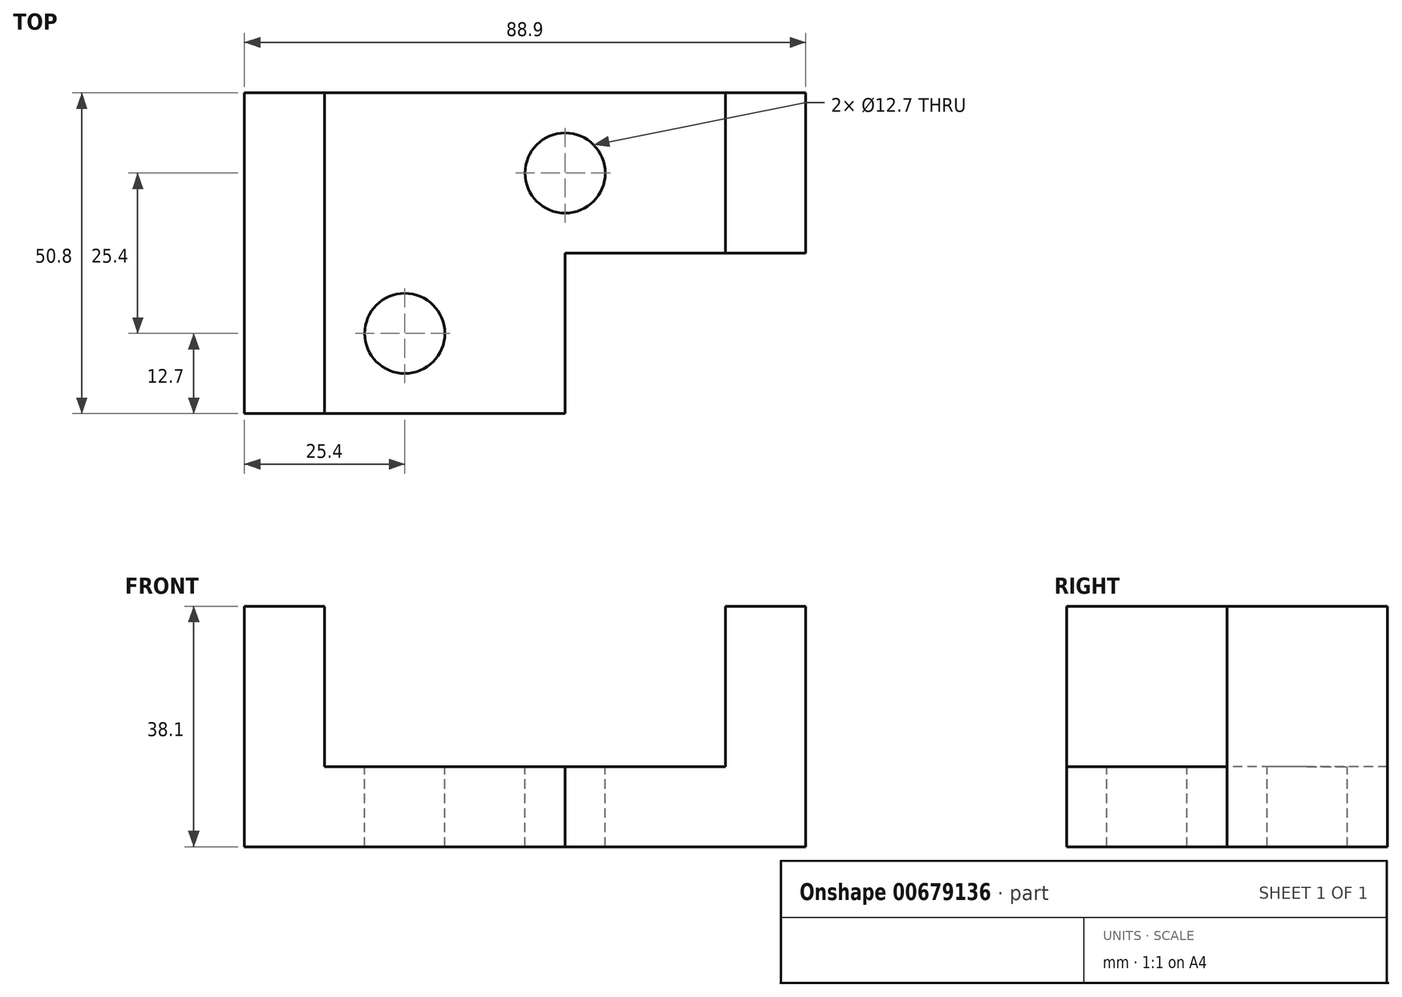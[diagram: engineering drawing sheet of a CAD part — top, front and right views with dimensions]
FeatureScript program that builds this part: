
annotation { "Feature Type Name" : "Feature", "Feature Type Description" : "" }
export const myFeature = defineFeature(function(context is Context, id is Id, definition is map)
    precondition{}
    {
        {
            var Q0;
            Q0=qCreatedBy(makeId("Front.planeOp"),FACE);
            var sketch = newSketch(context, id + "F0", { "sketchPlane" : qUnion([Q0])});
            skLineSegment(sketch, "E0.bottom", {"start": v(-44.45, 19.05) * mm, "end": v(44.45, 19.05) * mm});
            skLineSegment(sketch, "E0.top", {"start": v(-44.45, -19.05) * mm, "end": v(44.45, -19.05) * mm});
            skLineSegment(sketch, "E0.left", {"start": v(-44.45, 19.05) * mm, "end": v(-44.45, -19.05) * mm});
            skLineSegment(sketch, "E0.right", {"start": v(44.45, 19.05) * mm, "end": v(44.45, -19.05) * mm});
            skPoint(sketch, "E0.middle", {"position": v(0, 0) * mm});
            skSolve(sketch);
        }
        {
            var Q0;
            Q0=makeQuery(id+"F0.imprint","IMPRINT",FACE,{"disambiguationData":[TD([[makeQuery(id+"F0.imprint","IMPRINT",EDGE,{"derivedFrom":sQuery(id+"F0.wireOp",EDGE,"E0.bottom")}),-1.0]])]});
            extrude(context, id + "F1", {"entities" : qUnion([Q0]), "depth" : 50.8 * mm, "offsetDistance" : 25.4 * mm});
        }
        {
            var Q0;
            Q0=makeQuery(id+"F1.opExtrude","CAP_FACE",FACE,{"disambiguationData":[OSD([sQuery(id+"F0.wireOp",EDGE,"E0.bottom"),sQuery(id+"F0.wireOp",EDGE,"E0.top"),sQuery(id+"F0.wireOp",EDGE,"E0.left"),sQuery(id+"F0.wireOp",EDGE,"E0.right")])],"isStart":false});
            var sketch = newSketch(context, id + "F2", { "sketchPlane" : qUnion([Q0])});
            skLineSegment(sketch, "E1.bottom", {"start": v(-31.75, 19.05) * mm, "end": v(31.75, 19.05) * mm});
            skLineSegment(sketch, "E1.top", {"start": v(-31.75, 0) * mm, "end": v(31.75, 0) * mm});
            skLineSegment(sketch, "E1.left", {"start": v(-31.75, 19.05) * mm, "end": v(-31.75, 0) * mm});
            skLineSegment(sketch, "E1.right", {"start": v(31.75, 19.05) * mm, "end": v(31.75, 0) * mm});
            skSolve(sketch);
        }
        {
            var Q0;
            Q0=makeQuery(id+"F2.imprint","IMPRINT",FACE,{"disambiguationData":[TD([[makeQuery(id+"F2.imprint","IMPRINT",EDGE,{"derivedFrom":sQuery(id+"F2.wireOp",EDGE,"E1.bottom")}),-1.0]])]});
            extrude(context, id + "F3", {"entities" : qUnion([Q0]), "operationType" : NewBodyOperationType.REMOVE, "endBound" : BoundingType.THROUGH_ALL, "oppositeDirection" : true, "depth" : 25.4 * mm, "offsetDistance" : 25.4 * mm});
        }
        {
            var Q0;
            {var subQ0=sQuery(id+"F0.wireOp",EDGE,"E0.right");var subQ3=sQuery(id+"F0.wireOp",EDGE,"E0.bottom");Q0=makeQuery(id+"F3.boolean.opBoolean","SPLIT",FACE,{"disambiguationData":[TD([makeQuery(id+"F1.opExtrude","SWEPT_FACE",FACE,{"disambiguationData":[OSD([subQ0])]})])],"derivedFrom":makeQuery(id+"F1.opExtrude","SWEPT_FACE",FACE,{"disambiguationData":[OSD([subQ3])]})});}
            var sketch = newSketch(context, id + "F4", { "sketchPlane" : qUnion([Q0])});
            skLineSegment(sketch, "E2.bottom", {"start": v(44.45, -50.8) * mm, "end": v(6.35, -50.8) * mm});
            skLineSegment(sketch, "E2.top", {"start": v(44.45, -25.4) * mm, "end": v(6.35, -25.4) * mm});
            skLineSegment(sketch, "E2.left", {"start": v(44.45, -50.8) * mm, "end": v(44.45, -25.4) * mm});
            skLineSegment(sketch, "E2.right", {"start": v(6.35, -50.8) * mm, "end": v(6.35, -25.4) * mm});
            skSolve(sketch);
        }
        {
            var Q0;
            {var subQ0=sQuery(id+"F4.wireOp",EDGE,"E2.left");Q0=makeQuery(id+"F4.imprint","IMPRINT",FACE,{"disambiguationData":[TD([[makeQuery(id+"F4.imprint","IMPRINT",EDGE,{"derivedFrom":subQ0}),1.0]])]});}
            extrude(context, id + "F5", {"entities" : qUnion([Q0]), "operationType" : NewBodyOperationType.REMOVE, "endBound" : BoundingType.THROUGH_ALL, "oppositeDirection" : true, "depth" : 25.4 * mm, "offsetDistance" : 25.4 * mm});
        }
        {
            var Q0;
            Q0=makeQuery(id+"F3.boolean.opBoolean","COPY",FACE,{"derivedFrom":makeQuery(id+"F3.opExtrude","SWEPT_FACE",FACE,{"disambiguationData":[OSD([sQuery(id+"F2.wireOp",EDGE,"E1.top")])]})});
            var sketch = newSketch(context, id + "F6", { "sketchPlane" : qUnion([Q0])});
            skLineSegment(sketch, "E3.bottom", {"start": v(31.75, -50.8) * mm, "end": v(6.35, -50.8) * mm});
            skLineSegment(sketch, "E3.top", {"start": v(31.75, -25.4) * mm, "end": v(6.35, -25.4) * mm});
            skLineSegment(sketch, "E3.left", {"start": v(31.75, -50.8) * mm, "end": v(31.75, -25.4) * mm});
            skLineSegment(sketch, "E3.right", {"start": v(6.35, -50.8) * mm, "end": v(6.35, -25.4) * mm});
            skSolve(sketch);
        }
        {
            var Q0;
            Q0=makeQuery(id+"F6.imprint","IMPRINT",FACE,{"disambiguationData":[TD([[makeQuery(id+"F6.imprint","IMPRINT",EDGE,{"derivedFrom":sQuery(id+"F6.wireOp",EDGE,"E3.bottom")}),1.0]])]});
            extrude(context, id + "F7", {"entities" : qUnion([Q0]), "operationType" : NewBodyOperationType.REMOVE, "endBound" : BoundingType.THROUGH_ALL, "oppositeDirection" : true, "depth" : 25.4 * mm, "offsetDistance" : 25.4 * mm});
        }
        {
            var Q0;
            Q0=makeQuery(id+"F3.boolean.opBoolean","COPY",FACE,{"derivedFrom":makeQuery(id+"F3.opExtrude","SWEPT_FACE",FACE,{"disambiguationData":[OSD([sQuery(id+"F2.wireOp",EDGE,"E1.top")])]})});
            var sketch = newSketch(context, id + "F8", { "sketchPlane" : qUnion([Q0])});
            skCircle(sketch, "E4", {"center": v(-19.05, -38.1) * mm, "radius": 6.35 * mm});
            skSolve(sketch);
        }
        {
            var Q0;
            Q0=makeQuery(id+"F8.imprint","IMPRINT",FACE,{"disambiguationData":[TD([[makeQuery(id+"F8.imprint","IMPRINT",EDGE,{"derivedFrom":sQuery(id+"F8.wireOp",EDGE,"E4")}),1.0]])]});
            extrude(context, id + "F9", {"entities" : qUnion([Q0]), "operationType" : NewBodyOperationType.REMOVE, "endBound" : BoundingType.THROUGH_ALL, "oppositeDirection" : true, "depth" : 25.4 * mm, "offsetDistance" : 25.4 * mm});
        }
        {
            var Q0;
            Q0=makeQuery(id+"F3.boolean.opBoolean","COPY",FACE,{"derivedFrom":makeQuery(id+"F3.opExtrude","SWEPT_FACE",FACE,{"disambiguationData":[OSD([sQuery(id+"F2.wireOp",EDGE,"E1.top")])]})});
            var sketch = newSketch(context, id + "F10", { "sketchPlane" : qUnion([Q0])});
            skCircle(sketch, "E5", {"center": v(6.35, -12.7) * mm, "radius": 6.35 * mm});
            skSolve(sketch);
        }
        {
            var Q0;
            Q0=makeQuery(id+"F10.imprint","IMPRINT",FACE,{"disambiguationData":[TD([[makeQuery(id+"F10.imprint","IMPRINT",EDGE,{"derivedFrom":sQuery(id+"F10.wireOp",EDGE,"E5")}),1.0]])]});
            extrude(context, id + "F11", {"entities" : qUnion([Q0]), "operationType" : NewBodyOperationType.REMOVE, "endBound" : BoundingType.THROUGH_ALL, "oppositeDirection" : true, "depth" : 25.4 * mm, "offsetDistance" : 25.4 * mm});
        }
        {
            var Q0;
            Q0=makeQuery(id+"F1.opExtrude","CAP_FACE",FACE,{"disambiguationData":[OSD([sQuery(id+"F0.wireOp",EDGE,"E0.bottom"),sQuery(id+"F0.wireOp",EDGE,"E0.top"),sQuery(id+"F0.wireOp",EDGE,"E0.left"),sQuery(id+"F0.wireOp",EDGE,"E0.right")])],"isStart":false});
            var sketch = newSketch(context, id + "F12", { "sketchPlane" : qUnion([Q0])});
            skLineSegment(sketch, "E6.bottom", {"start": v(-31.75, 0) * mm, "end": v(6.35, 0) * mm});
            skLineSegment(sketch, "E6.top", {"start": v(-31.75, -6.35) * mm, "end": v(6.35, -6.35) * mm});
            skLineSegment(sketch, "E6.left", {"start": v(-31.75, 0) * mm, "end": v(-31.75, -6.35) * mm});
            skLineSegment(sketch, "E6.right", {"start": v(6.35, 0) * mm, "end": v(6.35, -6.35) * mm});
            skSolve(sketch);
        }
        {
            var Q0;
            Q0=makeQuery(id+"F12.imprint","IMPRINT",FACE,{"disambiguationData":[TD([[makeQuery(id+"F12.imprint","IMPRINT",EDGE,{"derivedFrom":sQuery(id+"F12.wireOp",EDGE,"E6.bottom")}),-1.0]])]});
            extrude(context, id + "F13", {"entities" : qUnion([Q0]), "operationType" : NewBodyOperationType.REMOVE, "endBound" : BoundingType.THROUGH_ALL, "oppositeDirection" : true, "depth" : 25.4 * mm, "offsetDistance" : 25.4 * mm});
        }
        {
            var Q0;
            Q0=makeQuery(id+"F7.boolean.opBoolean","MERGE",FACE,{"derivedFrom":[makeQuery(id+"F5.boolean.opBoolean","COPY",FACE,{"derivedFrom":makeQuery(id+"F5.opExtrude","SWEPT_FACE",FACE,{"disambiguationData":[OSD([sQuery(id+"F4.wireOp",EDGE,"E2.top")])]})}),makeQuery(id+"F7.opExtrude","SWEPT_FACE",FACE,{"disambiguationData":[OSD([sQuery(id+"F6.wireOp",EDGE,"E3.top")])]})]});
            var sketch = newSketch(context, id + "F14", { "sketchPlane" : qUnion([Q0])});
            skLineSegment(sketch, "E7.bottom", {"start": v(31.75, 0) * mm, "end": v(6.35, 0) * mm});
            skLineSegment(sketch, "E7.top", {"start": v(31.75, -6.35) * mm, "end": v(6.35, -6.35) * mm});
            skLineSegment(sketch, "E7.left", {"start": v(31.75, 0) * mm, "end": v(31.75, -6.35) * mm});
            skLineSegment(sketch, "E7.right", {"start": v(6.35, 0) * mm, "end": v(6.35, -6.35) * mm});
            skSolve(sketch);
        }
        {
            var Q0;
            Q0=makeQuery(id+"F14.imprint","IMPRINT",FACE,{"disambiguationData":[TD([[makeQuery(id+"F14.imprint","IMPRINT",EDGE,{"derivedFrom":sQuery(id+"F14.wireOp",EDGE,"E7.bottom")}),1.0]])]});
            extrude(context, id + "F15", {"entities" : qUnion([Q0]), "operationType" : NewBodyOperationType.REMOVE, "endBound" : BoundingType.THROUGH_ALL, "oppositeDirection" : true, "depth" : 25.4 * mm, "offsetDistance" : 25.4 * mm});
        }
    });
